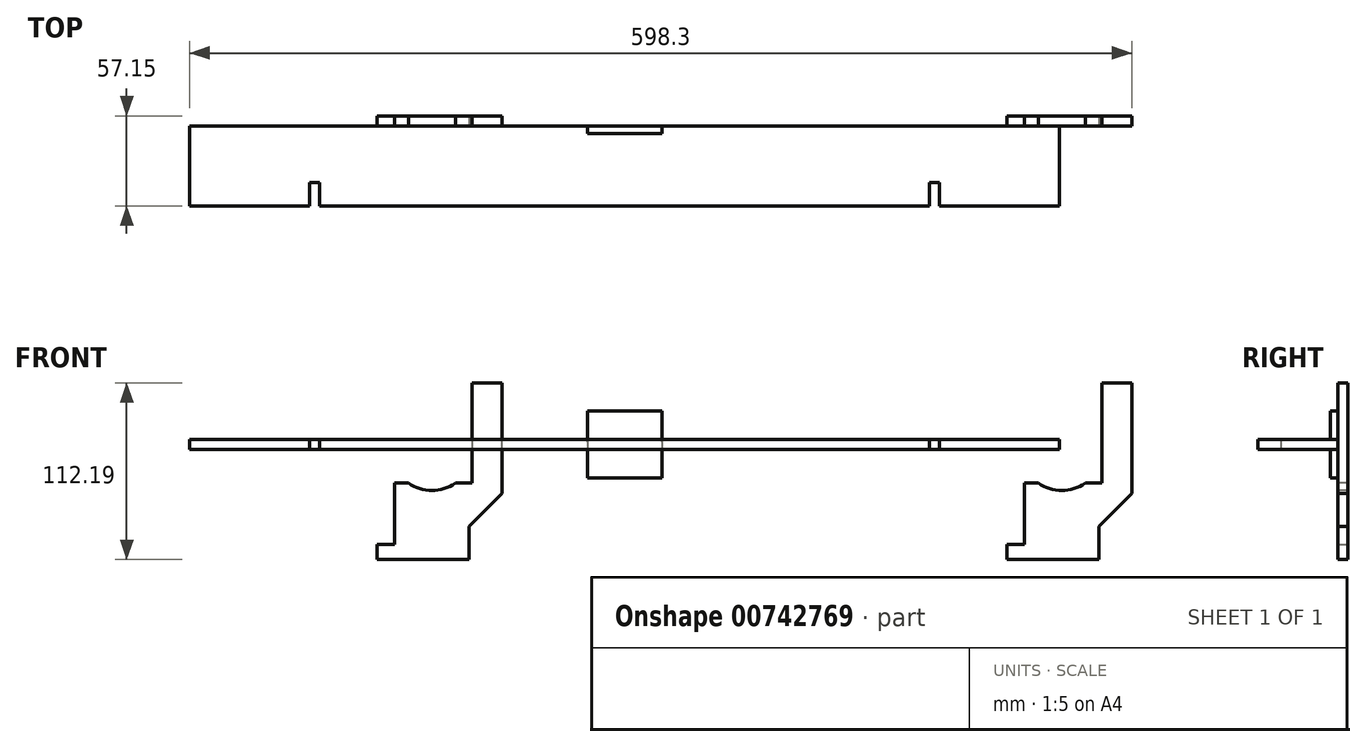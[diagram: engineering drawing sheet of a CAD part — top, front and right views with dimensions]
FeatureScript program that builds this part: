
annotation { "Feature Type Name" : "Feature", "Feature Type Description" : "" }
export const myFeature = defineFeature(function(context is Context, id is Id, definition is map)
    precondition{}
    {
        {
            var Q0;
            Q0=qCreatedBy(makeId("Top.planeOp"),FACE);
            var sketch = newSketch(context, id + "F0", { "sketchPlane" : qUnion([Q0])});
            skLineSegment(sketch, "E0.0", {"start": v(31.75, 160.54) * mm, "end": v(584.2, 160.54) * mm});
            skLineSegment(sketch, "E1.0", {"start": v(107.95, 109.74) * mm, "end": v(107.95, 124.54) * mm});
            skLineSegment(sketch, "E2.0", {"start": v(114.3, 109.74) * mm, "end": v(114.3, 124.54) * mm});
            skLineSegment(sketch, "E3.0", {"start": v(508, 109.74) * mm, "end": v(508, 124.54) * mm});
            skLineSegment(sketch, "E4.0", {"start": v(501.65, 109.74) * mm, "end": v(501.65, 124.54) * mm});
            skLineSegment(sketch, "E5.0", {"start": v(584.2, 109.74) * mm, "end": v(584.2, 160.54) * mm});
            skLineSegment(sketch, "E6.0", {"start": v(31.75, 109.74) * mm, "end": v(31.75, 160.54) * mm});
            skLineSegment(sketch, "E7.0", {"start": v(31.75, 109.74) * mm, "end": v(107.95, 109.74) * mm});
            skLineSegment(sketch, "E8.trimOffspring", {"start": v(114.3, 109.74) * mm, "end": v(501.65, 109.74) * mm});
            skLineSegment(sketch, "E9.trimOffspring", {"start": v(508, 109.74) * mm, "end": v(584.2, 109.74) * mm});
            skLineSegment(sketch, "E10.0", {"start": v(107.95, 124.54) * mm, "end": v(114.3, 124.54) * mm});
            skLineSegment(sketch, "E11.trimOffspring", {"start": v(501.65, 124.54) * mm, "end": v(508, 124.54) * mm});
            skSolve(sketch);
        }
        {
            var Q0;
            Q0=qSketchRegion(id+"F0",true);
            extrude(context, id + "F1", {"entities" : qUnion([Q0]), "depth" : 6.35 * mm, "offsetDistance" : 25.4 * mm});
        }
        {
            var Q0;
            Q0=makeQuery(id+"F1.opExtrude","CAP_FACE",FACE,{"disambiguationData":[OSD([sQuery(id+"F0.wireOp",EDGE,"E0.0"),sQuery(id+"F0.wireOp",EDGE,"E1.0"),sQuery(id+"F0.wireOp",EDGE,"E2.0"),sQuery(id+"F0.wireOp",EDGE,"E3.0"),sQuery(id+"F0.wireOp",EDGE,"E4.0"),sQuery(id+"F0.wireOp",EDGE,"E5.0"),sQuery(id+"F0.wireOp",EDGE,"E6.0"),sQuery(id+"F0.wireOp",EDGE,"E7.0"),sQuery(id+"F0.wireOp",EDGE,"E8.trimOffspring"),sQuery(id+"F0.wireOp",EDGE,"E9.trimOffspring"),sQuery(id+"F0.wireOp",EDGE,"E10.0"),sQuery(id+"F0.wireOp",EDGE,"E11.trimOffspring")])],"isStart":true});
            var sketch = newSketch(context, id + "F2", { "sketchPlane" : qUnion([Q0])});
            skLineSegment(sketch, "E12.bottom", {"start": v(331.6, -160.54) * mm, "end": v(284.35, -160.54) * mm});
            skLineSegment(sketch, "E12.top", {"start": v(331.6, -155.78) * mm, "end": v(284.35, -155.78) * mm});
            skLineSegment(sketch, "E12.left", {"start": v(331.6, -160.54) * mm, "end": v(331.6, -155.78) * mm});
            skLineSegment(sketch, "E12.right", {"start": v(284.35, -160.54) * mm, "end": v(284.35, -155.78) * mm});
            skSolve(sketch);
        }
        {
            var Q0;
            Q0=qSketchRegion(id+"F2",true);
            extrude(context, id + "F3", {"entities" : qUnion([Q0]), "operationType" : NewBodyOperationType.REMOVE, "oppositeDirection" : true, "depth" : 36.25 * mm, "offsetDistance" : 25.4 * mm});
        }
        {
            var Q0;
            Q0=makeQuery(id+"F3.boolean.opBoolean","COPY",FACE,{"derivedFrom":makeQuery(id+"F3.opExtrude","SWEPT_FACE",FACE,{"disambiguationData":[OSD([sQuery(id+"F2.wireOp",EDGE,"E12.top")])]})});
            var sketch = newSketch(context, id + "F4", { "sketchPlane" : qUnion([Q0])});
            skLineSegment(sketch, "E13.bottom", {"start": v(-284.35, -18.12) * mm, "end": v(-331.6, -18.12) * mm});
            skLineSegment(sketch, "E13.top", {"start": v(-284.35, 24.47) * mm, "end": v(-331.6, 24.47) * mm});
            skLineSegment(sketch, "E13.left", {"start": v(-284.35, -18.12) * mm, "end": v(-284.35, 24.47) * mm});
            skLineSegment(sketch, "E13.right", {"start": v(-331.6, -18.12) * mm, "end": v(-331.6, 24.47) * mm});
            skSolve(sketch);
        }
        {
            var Q0;
            Q0=qSketchRegion(id+"F4",true);
            extrude(context, id + "F5", {"entities" : qUnion([Q0]), "operationType" : NewBodyOperationType.ADD, "depth" : 4.78 * mm, "offsetDistance" : 25.4 * mm});
        }
        {
            var Q0;
            {var subQ6=sQuery(id+"F0.wireOp",EDGE,"E5.0");var subQ11=sQuery(id+"F0.wireOp",EDGE,"E0.0");Q0=makeQuery(id+"F3.boolean.opBoolean","SPLIT",FACE,{"disambiguationData":[TD([makeQuery(id+"F1.opExtrude","SWEPT_FACE",FACE,{"disambiguationData":[OSD([subQ6])]})])],"derivedFrom":makeQuery(id+"F1.opExtrude","SWEPT_FACE",FACE,{"disambiguationData":[OSD([subQ11])]})});}
            var sketch = newSketch(context, id + "F6", { "sketchPlane" : qUnion([Q0])});
            skLineSegment(sketch, "E14.bottom", {"start": v(-561.98, -27.5) * mm, "end": v(-609.22, -27.5) * mm});
            skLineSegment(sketch, "E14.top", {"start": v(-561.98, -69.85) * mm, "end": v(-609.22, -69.85) * mm});
            skLineSegment(sketch, "E14.left", {"start": v(-561.98, -27.5) * mm, "end": v(-561.98, -69.85) * mm});
            skLineSegment(sketch, "E14.right", {"start": v(-609.22, -27.5) * mm, "end": v(-609.22, -69.85) * mm});
            skLineSegment(sketch, "E15", {"start": v(-609.22, -48.68) * mm, "end": v(-630.05, -27.85) * mm});
            skLineSegment(sketch, "E16", {"start": v(-630.05, -27.85) * mm, "end": v(-630.05, 42.34) * mm});
            skLineSegment(sketch, "E17", {"start": v(-630.05, 42.34) * mm, "end": v(-611, 42.34) * mm});
            skLineSegment(sketch, "E18", {"start": v(-611, 42.34) * mm, "end": v(-611, -21.16) * mm});
            skLineSegment(sketch, "E19", {"start": v(-611, -21.16) * mm, "end": v(-600.5, -21.16) * mm});
            skLineSegment(sketch, "E20", {"start": v(-561.97, -21.16) * mm, "end": v(-561.98, -27.5) * mm});
            skArc(sketch, "E21", {"start": v(-600.5, -21.16) * mm, "mid": v(-585.6, -25.98) * mm, "end": v(-570.7, -21.16) * mm});
            skLineSegment(sketch, "E22.trimOffspring", {"start": v(-570.7, -21.16) * mm, "end": v(-561.97, -21.16) * mm});
            skSolve(sketch);
        }
        {
            var Q0;
            Q0=qSketchRegion(id+"F6",true);
            extrude(context, id + "F7", {"entities" : qUnion([Q0]), "operationType" : NewBodyOperationType.ADD, "depth" : 6.35 * mm, "offsetDistance" : 25.4 * mm});
        }
        {
            var Q0;
            Q0=makeQuery(id+"F7.opExtrude","SWEPT_FACE",FACE,{"disambiguationData":[OSD([sQuery(id+"F6.wireOp",EDGE,"E14.left")])]});
            var sketch = newSketch(context, id + "F8", { "sketchPlane" : qUnion([Q0])});
            skLineSegment(sketch, "E23.bottom", {"start": v(-160.54, -69.85) * mm, "end": v(-166.9, -69.85) * mm});
            skLineSegment(sketch, "E23.top", {"start": v(-160.54, -60.32) * mm, "end": v(-166.9, -60.32) * mm});
            skLineSegment(sketch, "E23.left", {"start": v(-160.54, -69.85) * mm, "end": v(-160.54, -60.32) * mm});
            skLineSegment(sketch, "E23.right", {"start": v(-166.9, -69.85) * mm, "end": v(-166.9, -60.32) * mm});
            skSolve(sketch);
        }
        {
            var Q0;
            Q0=qSketchRegion(id+"F8",true);
            extrude(context, id + "F9", {"entities" : qUnion([Q0]), "operationType" : NewBodyOperationType.ADD, "depth" : 11.3 * mm, "offsetDistance" : 25.4 * mm});
        }
        {
            var Q0;
            Q0=makeQuery(id+"F7.opExtrude","SWEPT_BODY",BODY,{"disambiguationData":[OSD([sQuery(id+"F6.wireOp",EDGE,"E14.top"),sQuery(id+"F6.wireOp",EDGE,"E14.left"),sQuery(id+"F6.wireOp",EDGE,"E14.right"),sQuery(id+"F6.wireOp",EDGE,"E15"),sQuery(id+"F6.wireOp",EDGE,"E16"),sQuery(id+"F6.wireOp",EDGE,"E17"),sQuery(id+"F6.wireOp",EDGE,"E18"),sQuery(id+"F6.wireOp",EDGE,"E19"),sQuery(id+"F6.wireOp",EDGE,"E20"),sQuery(id+"F6.wireOp",EDGE,"E21"),sQuery(id+"F6.wireOp",EDGE,"E22.trimOffspring")])]});
            transform(context, id + "F10", {"entities" : qUnion([Q0]), "transformType" : TransformType.TRANSLATION_3D, "dx" : -400.05 * mm, "dy" : 0 * mm, "dz" : 0 * mm, "makeCopy" : true});
        }
    });
